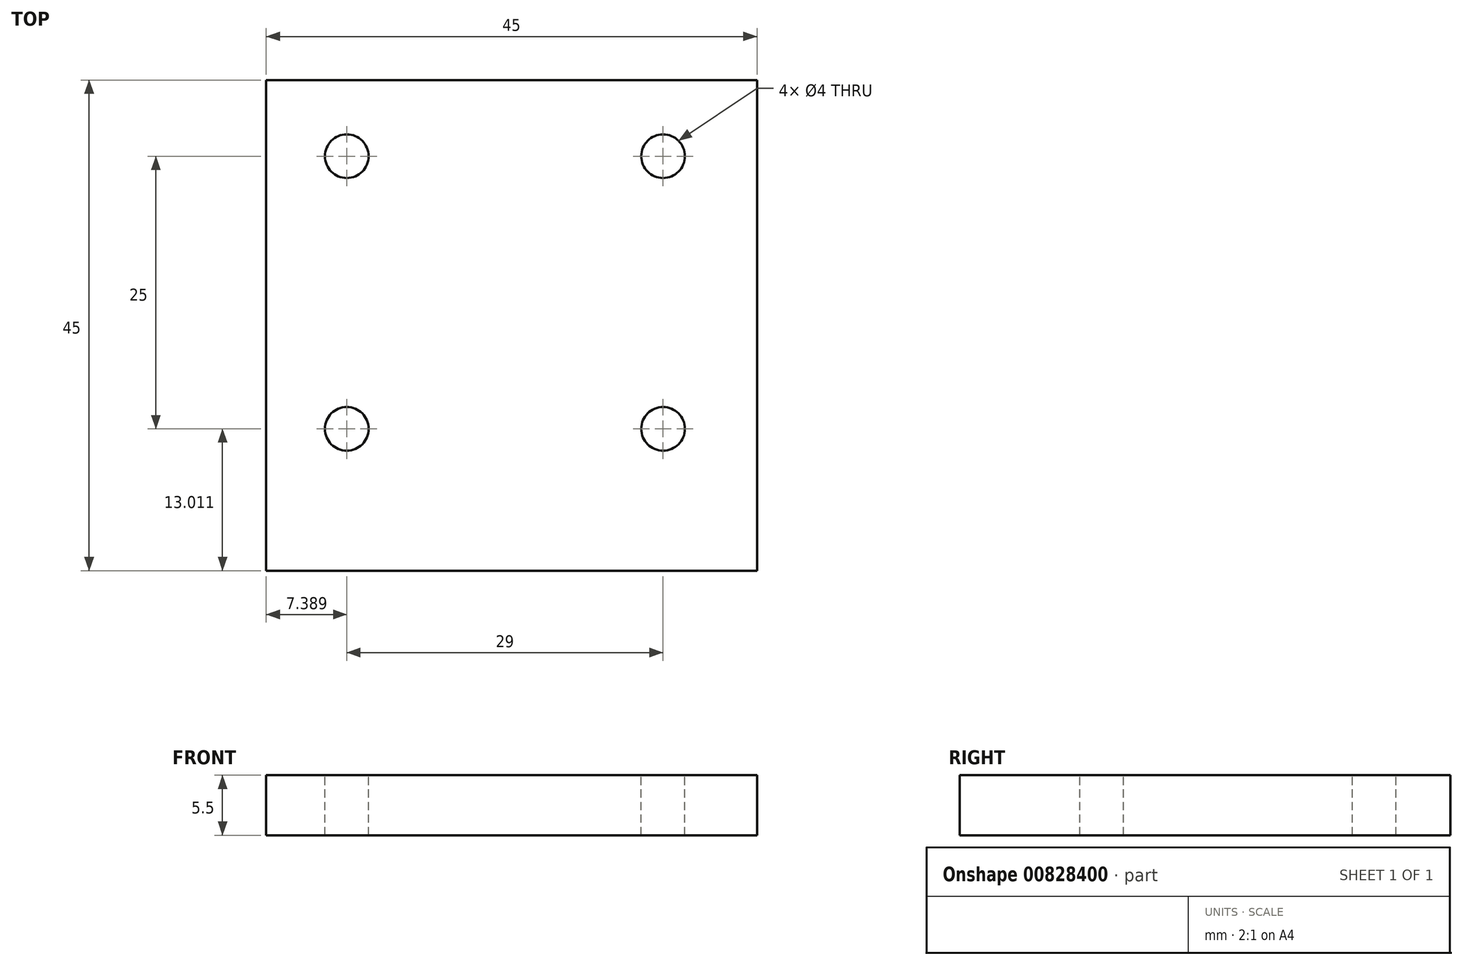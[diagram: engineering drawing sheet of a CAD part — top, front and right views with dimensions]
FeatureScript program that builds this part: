
annotation { "Feature Type Name" : "Feature", "Feature Type Description" : "" }
export const myFeature = defineFeature(function(context is Context, id is Id, definition is map)
    precondition{}
    {
        {
            var Q0;
            Q0=qCreatedBy(makeId("Top.planeOp"),FACE);
            var sketch = newSketch(context, id + "F0", { "sketchPlane" : qUnion([Q0])});
            skLineSegment(sketch, "E0.bottom", {"start": v(-22.5, 22.5) * mm, "end": v(22.5, 22.5) * mm});
            skLineSegment(sketch, "E0.top", {"start": v(-22.5, -22.5) * mm, "end": v(22.5, -22.5) * mm});
            skLineSegment(sketch, "E0.left", {"start": v(-22.5, 22.5) * mm, "end": v(-22.5, -22.5) * mm});
            skLineSegment(sketch, "E0.right", {"start": v(22.5, 22.5) * mm, "end": v(22.5, -22.5) * mm});
            skSolve(sketch);
        }
        {
            var Q0;
            Q0 = qSketchRegion(id + "F0", true);
            extrude(context, id + "F1", {"entities" : qUnion([Q0]), "depth" : 5.5 * mm, "offsetDistance" : 25 * mm});
        }
        {
            var Q0;
            Q0=makeQuery(id+"F1.opExtrude","CAP_FACE",FACE,{"disambiguationData":[OSD([sQuery(id+"F0.wireOp",EDGE,"E0.bottom"),sQuery(id+"F0.wireOp",EDGE,"E0.top"),sQuery(id+"F0.wireOp",EDGE,"E0.left"),sQuery(id+"F0.wireOp",EDGE,"E0.right")])],"isStart":false});
            var sketch = newSketch(context, id + "F2", { "sketchPlane" : qUnion([Q0])});
            skCircle(sketch, "E1", {"center": v(-15.11, 15.51) * mm, "radius": 2 * mm});
            skCircle(sketch, "E2.0.1.0", {"center": v(-15.11, -9.49) * mm, "radius": 2 * mm});
            skCircle(sketch, "E2.1.0.0", {"center": v(13.89, 15.51) * mm, "radius": 2 * mm});
            skCircle(sketch, "E2.1.1.0", {"center": v(13.89, -9.49) * mm, "radius": 2 * mm});
            skLineSegment(sketch, "E2.direction1", {"start": v(-15.11, 15.51) * mm, "end": v(13.89, 15.51) * mm, "construction": true});
            skLineSegment(sketch, "E2.direction2", {"start": v(-15.11, 15.51) * mm, "end": v(-15.11, -9.49) * mm, "construction": true});
            skSolve(sketch);
        }
        {
            var Q0;
            Q0 = qSketchRegion(id + "F2", true);
            extrude(context, id + "F3", {"entities" : qUnion([Q0]), "operationType" : NewBodyOperationType.REMOVE, "endBound" : BoundingType.THROUGH_ALL, "oppositeDirection" : true, "depth" : 25 * mm, "offsetDistance" : 25 * mm});
        }
    });
